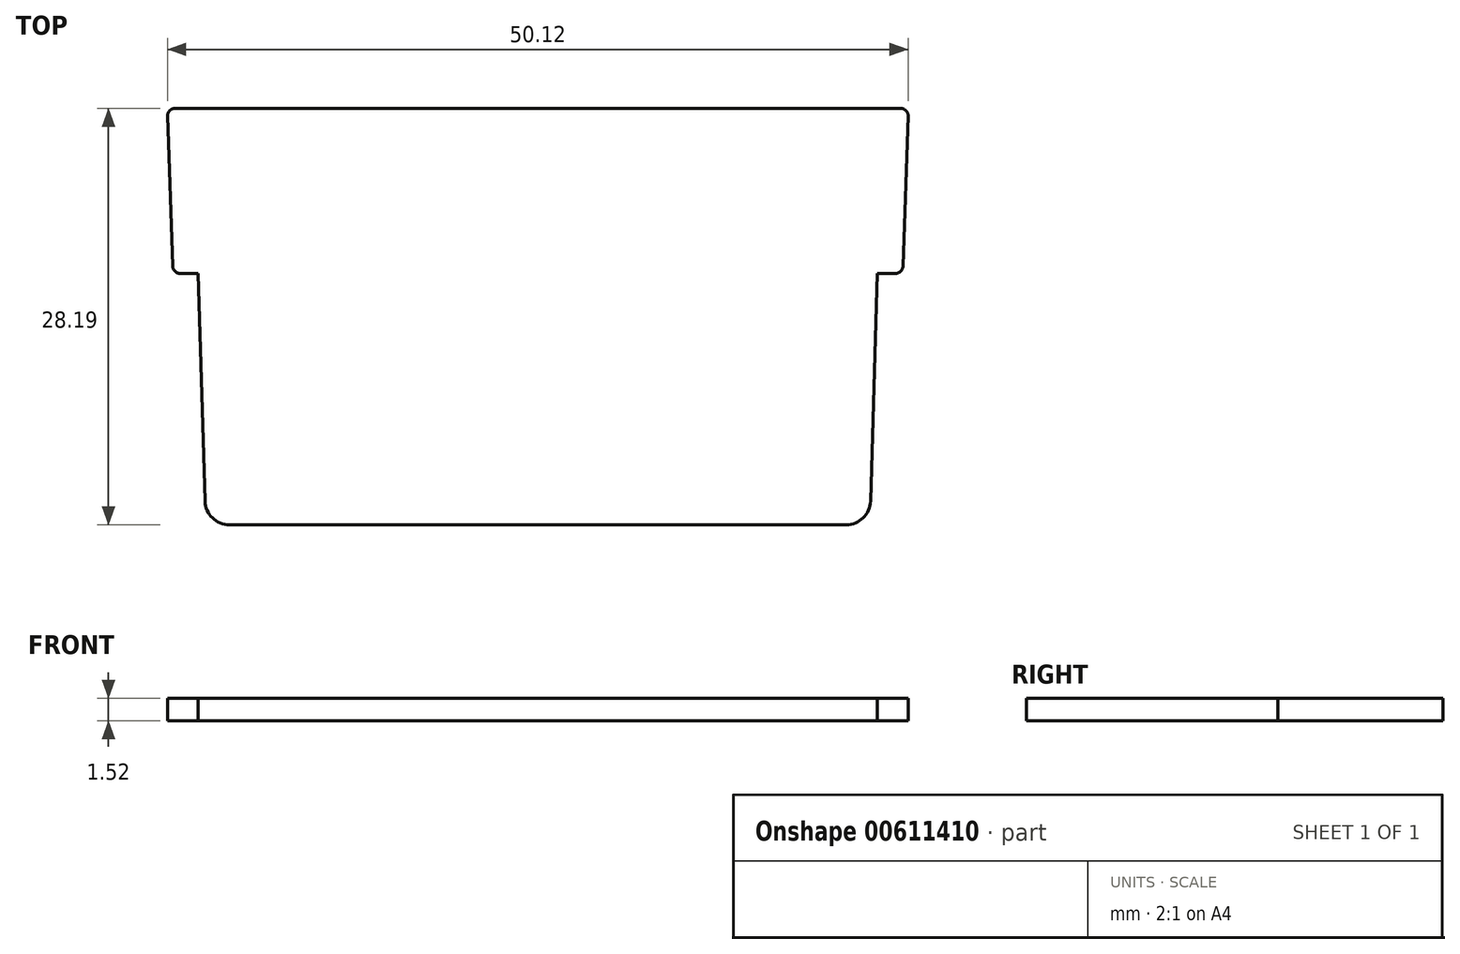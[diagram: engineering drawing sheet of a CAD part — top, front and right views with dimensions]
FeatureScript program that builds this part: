
annotation { "Feature Type Name" : "Feature", "Feature Type Description" : "" }
export const myFeature = defineFeature(function(context is Context, id is Id, definition is map)
    precondition{}
    {
        {
            var Q0;
            Q0=qCreatedBy(makeId("Top.planeOp"),FACE);
            var sketch = newSketch(context, id + "F0", { "sketchPlane" : qUnion([Q0])});
            skLineSegment(sketch, "E0.bottom", {"start": v(-22.48, 0) * mm, "end": v(22.48, 0) * mm});
            skLineSegment(sketch, "E0.left", {"start": v(-22.48, 0) * mm, "end": v(-22.99, 17.02) * mm});
            skLineSegment(sketch, "E0.right", {"start": v(22.48, 0) * mm, "end": v(22.99, 17.02) * mm});
            skLineSegment(sketch, "E1", {"start": v(-22.99, 17.02) * mm, "end": v(-24.7, 17.02) * mm});
            skLineSegment(sketch, "E2", {"start": v(-24.7, 17.02) * mm, "end": v(-25.08, 28.2) * mm});
            skLineSegment(sketch, "E3", {"start": v(-25.08, 28.2) * mm, "end": v(25.08, 28.2) * mm});
            skLineSegment(sketch, "E4", {"start": v(25.08, 28.2) * mm, "end": v(24.7, 17.02) * mm});
            skLineSegment(sketch, "E5", {"start": v(24.7, 17.02) * mm, "end": v(22.99, 17.02) * mm});
            skLineSegment(sketch, "E6", {"start": v(0, 0) * mm, "end": v(0, 28.2) * mm, "construction": true});
            skLineSegment(sketch, "E7", {"start": v(-22.99, 17.02) * mm, "end": v(22.99, 17.02) * mm, "construction": true});
            skLineSegment(sketch, "E8", {"start": v(0, 17.02) * mm, "end": v(0, 0) * mm, "construction": true});
            skSolve(sketch);
        }
        {
            var Q0;
            Q0 = qSketchRegion(id + "F0", true);
            extrude(context, id + "F1", {"entities" : qUnion([Q0]), "depth" : 1.52 * mm, "offsetDistance" : 25.4 * mm});
        }
        {
            var Q0;
            Q0=makeQuery(id+"F1.opExtrude","SWEPT_EDGE",EDGE,{"disambiguationData":[OSD([sQuery(id+"F0.wireOp",EDGE,"E3"),sQuery(id+"F0.wireOp",EDGE,"E4")])]});
            var Q1;
            Q1=makeQuery(id+"F1.opExtrude","SWEPT_EDGE",EDGE,{"disambiguationData":[OSD([sQuery(id+"F0.wireOp",EDGE,"E4"),sQuery(id+"F0.wireOp",EDGE,"E5")])]});
            var Q2;
            Q2=makeQuery(id+"F1.opExtrude","SWEPT_EDGE",EDGE,{"disambiguationData":[OSD([sQuery(id+"F0.wireOp",EDGE,"E2"),sQuery(id+"F0.wireOp",EDGE,"E3")])]});
            var Q3;
            Q3=makeQuery(id+"F1.opExtrude","SWEPT_EDGE",EDGE,{"disambiguationData":[OSD([sQuery(id+"F0.wireOp",EDGE,"E1"),sQuery(id+"F0.wireOp",EDGE,"E2")])]});
            fillet(context, id + "F2", {"entities" : qUnion([Q0, Q1, Q2, Q3]), "radius" : 0.5 * mm, "tangentPropagation" : true, "allowEdgeOverflow" : false});
        }
        {
            var Q0;
            Q0=makeQuery(id+"F1.opExtrude","SWEPT_EDGE",EDGE,{"disambiguationData":[OSD([sQuery(id+"F0.wireOp",EDGE,"E0.bottom"),sQuery(id+"F0.wireOp",EDGE,"E0.left")])]});
            var Q1;
            Q1=makeQuery(id+"F1.opExtrude","SWEPT_EDGE",EDGE,{"disambiguationData":[OSD([sQuery(id+"F0.wireOp",EDGE,"E0.bottom"),sQuery(id+"F0.wireOp",EDGE,"E0.right")])]});
            fillet(context, id + "F3", {"entities" : qUnion([Q0, Q1]), "radius" : 1.65 * mm, "tangentPropagation" : true, "allowEdgeOverflow" : false});
        }
    });
